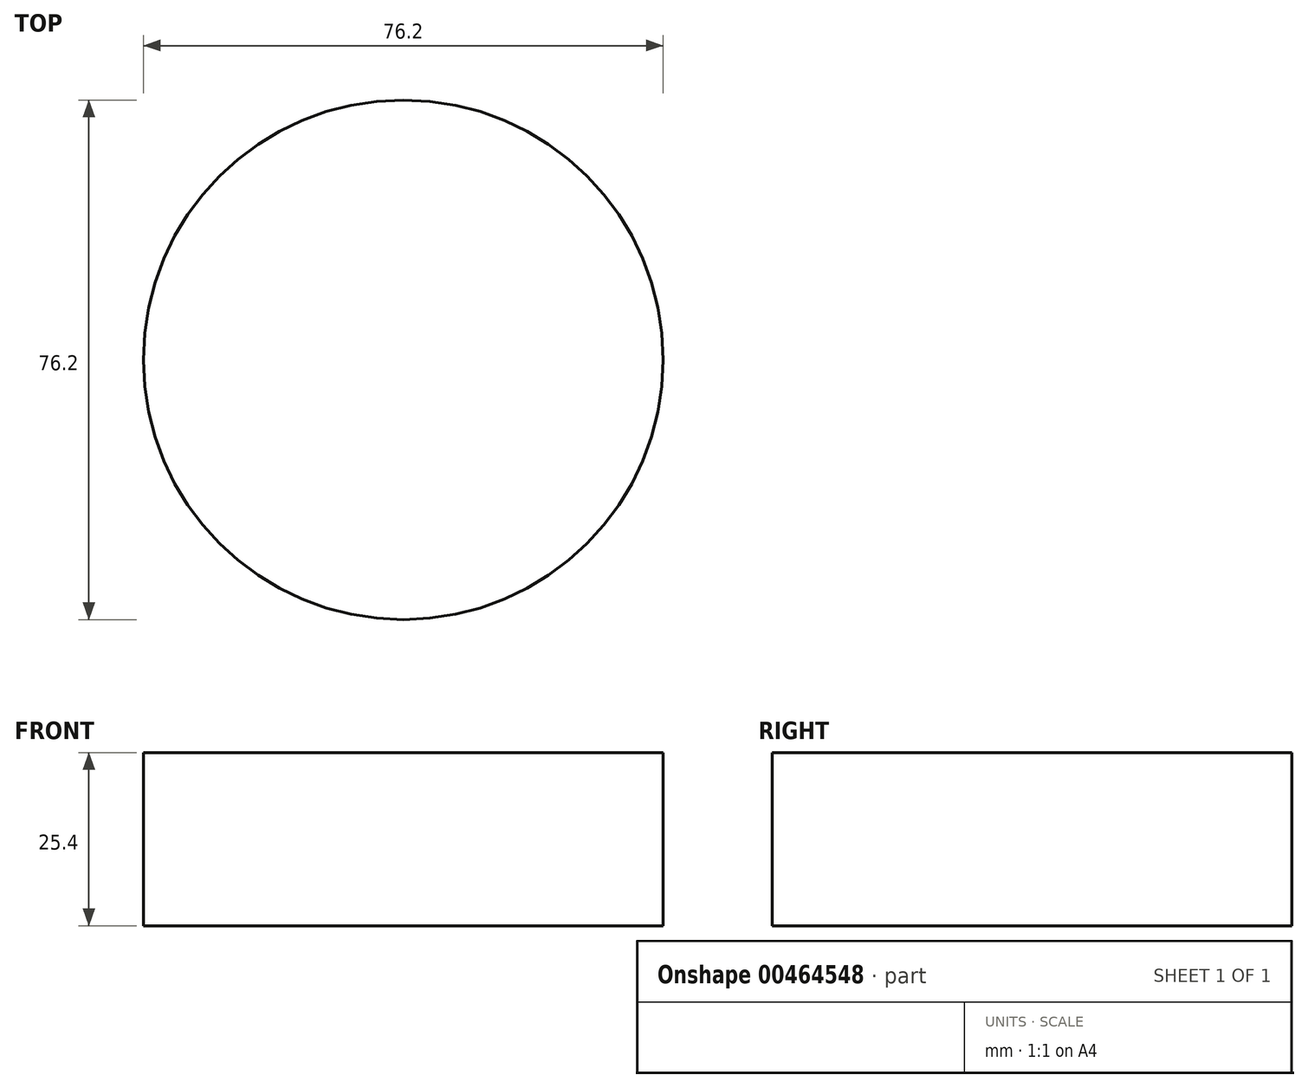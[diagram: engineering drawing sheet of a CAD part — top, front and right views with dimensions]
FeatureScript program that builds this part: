
annotation { "Feature Type Name" : "Feature", "Feature Type Description" : "" }
export const myFeature = defineFeature(function(context is Context, id is Id, definition is map)
    precondition{}
    {
        {
            var Q0;
            Q0=qCreatedBy(makeId("Top.planeOp"),FACE);
            var sketch = newSketch(context, id + "F0", { "sketchPlane" : qUnion([Q0])});
            skCircle(sketch, "E0", {"center": v(0, 0) * mm, "radius": 38.1 * mm});
            skSolve(sketch);
        }
        {
            var Q0;
            Q0=makeQuery(id+"F0.imprint","IMPRINT",FACE,{"disambiguationData":[TD([[makeQuery(id+"F0.imprint","IMPRINT",EDGE,{"derivedFrom":sQuery(id+"F0.wireOp",EDGE,"E0")}),1.0]])]});
            extrude(context, id + "F1", {"entities" : qUnion([Q0]), "depth" : 25.4 * mm});
        }
    });
